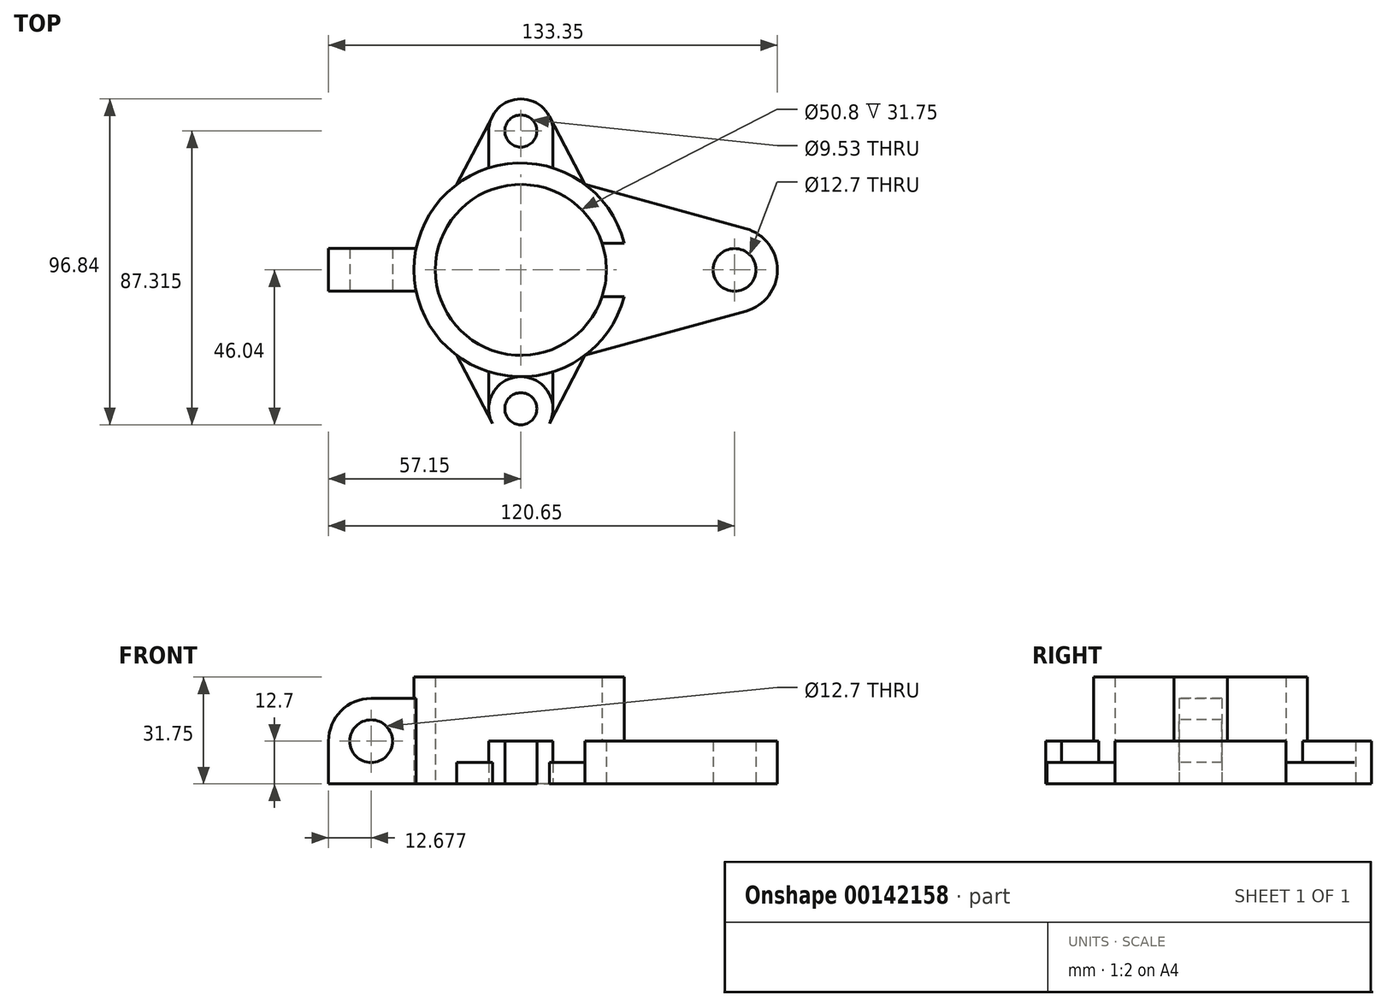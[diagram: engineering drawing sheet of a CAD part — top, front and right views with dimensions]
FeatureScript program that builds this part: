
annotation { "Feature Type Name" : "Feature", "Feature Type Description" : "" }
export const myFeature = defineFeature(function(context is Context, id is Id, definition is map)
    precondition{}
    {
        {
            var Q0;
            Q0=qCreatedBy(makeId("Top.planeOp"),FACE);
            var sketch = newSketch(context, id + "F0", { "sketchPlane" : qUnion([Q0])});
            skCircle(sketch, "E0", {"center": v(0, 0) * mm, "radius": 31.75 * mm});
            skCircle(sketch, "E1", {"center": v(0, 0) * mm, "radius": 25.4 * mm});
            skCircle(sketch, "E2", {"center": v(0, 41.28) * mm, "radius": 4.76 * mm});
            skCircle(sketch, "E3", {"center": v(0, 41.28) * mm, "radius": 9.53 * mm});
            skLineSegment(sketch, "E4", {"start": v(19.05, 25.4) * mm, "end": v(8.44, 45.69) * mm});
            skLineSegment(sketch, "E5.MirrorCS", {"start": v(-19.05, 25.4) * mm, "end": v(-8.44, 45.69) * mm});
            skLineSegment(sketch, "E6", {"start": v(9.53, 30.29) * mm, "end": v(9.53, 41.28) * mm});
            skLineSegment(sketch, "E7.MirrorCS", {"start": v(-9.53, 30.29) * mm, "end": v(-9.53, 41.28) * mm});
            skLineSegment(sketch, "E8.MirrorCS", {"start": v(-9.53, -30.29) * mm, "end": v(-9.53, -41.28) * mm});
            skLineSegment(sketch, "E9.MirrorCS", {"start": v(-19.05, -25.4) * mm, "end": v(-8.44, -45.69) * mm});
            skLineSegment(sketch, "E10.MirrorCS", {"start": v(9.53, -30.29) * mm, "end": v(9.53, -41.28) * mm});
            skLineSegment(sketch, "E11.MirrorCS", {"start": v(19.05, -25.4) * mm, "end": v(8.44, -45.69) * mm});
            skCircle(sketch, "E12.MirrorC", {"center": v(0, -41.28) * mm, "radius": 9.53 * mm});
            skCircle(sketch, "E13.MirrorC", {"center": v(0, -41.28) * mm, "radius": 4.76 * mm});
            skArc(sketch, "E14", {"start": v(66.87, -12.25) * mm, "mid": v(76.2, 0) * mm, "end": v(66.87, 12.25) * mm});
            skCircle(sketch, "E15", {"center": v(63.5, 0) * mm, "radius": 6.35 * mm});
            skLineSegment(sketch, "E16", {"start": v(19.05, -25.4) * mm, "end": v(66.87, -12.25) * mm});
            skLineSegment(sketch, "E17.MirrorCS", {"start": v(19.05, 25.4) * mm, "end": v(66.87, 12.25) * mm});
            skLineSegment(sketch, "E18.0", {"start": v(-31.1, 6.35) * mm, "end": v(-57.15, 6.35) * mm});
            skCircle(sketch, "E19", {"center": v(0, 0) * mm, "radius": 44.45 * mm, "construction": true});
            skCircle(sketch, "E20", {"center": v(-44.45, 0) * mm, "radius": 12.7 * mm, "construction": true});
            skLineSegment(sketch, "E21", {"start": v(-57.15, 0) * mm, "end": v(-57.15, 6.35) * mm});
            skLineSegment(sketch, "E22.MirrorCS", {"start": v(-57.15, 0) * mm, "end": v(-57.15, -6.35) * mm});
            skLineSegment(sketch, "E23.MirrorCS", {"start": v(-31.1, -6.35) * mm, "end": v(-57.15, -6.35) * mm});
            skSolve(sketch);
        }
        {
            var Q0;
            Q0=makeQuery(id+"F0.imprint","IMPRINT",FACE,{"disambiguationData":[TD([[makeQuery(id+"F0.imprint","IMPRINT",EDGE,{"derivedFrom":sQuery(id+"F0.wireOp",EDGE,"E1")}),-1.0]])]});
            extrude(context, id + "F1", {"entities" : qUnion([Q0]), "depth" : 31.75 * mm});
        }
        {
            var Q0;
            Q0=makeQuery(id+"F0.imprint","IMPRINT",FACE,{"disambiguationData":[TD([[makeQuery(id+"F0.imprint","IMPRINT",EDGE,{"derivedFrom":sQuery(id+"F0.wireOp",EDGE,"E2")}),-1.0]])]});
            var Q1;
            {var subQ0=sQuery(id+"F0.wireOp",EDGE,"E6");Q1=makeQuery(id+"F0.imprint","IMPRINT",FACE,{"disambiguationData":[TD([[makeQuery(id+"F0.imprint","IMPRINT",EDGE,{"derivedFrom":subQ0}),1.0]])]});}
            var Q2;
            {var subQ0=sQuery(id+"F0.wireOp",EDGE,"E10.MirrorCS");Q2=makeQuery(id+"F0.imprint","IMPRINT",FACE,{"disambiguationData":[TD([[makeQuery(id+"F0.imprint","IMPRINT",EDGE,{"derivedFrom":subQ0}),-1.0]])]});}
            var Q3;
            {var subQ0=sQuery(id+"F0.wireOp",EDGE,"E8.MirrorCS");Q3=makeQuery(id+"F0.imprint","IMPRINT",FACE,{"disambiguationData":[TD([[makeQuery(id+"F0.imprint","IMPRINT",EDGE,{"derivedFrom":subQ0}),1.0]])]});}
            var Q4;
            Q4=makeQuery(id+"F0.imprint","IMPRINT",FACE,{"disambiguationData":[TD([[makeQuery(id+"F0.imprint","IMPRINT",EDGE,{"derivedFrom":sQuery(id+"F0.wireOp",EDGE,"E13.MirrorC")}),1.0]])]});
            var Q5;
            {var subQ0=sQuery(id+"F0.wireOp",EDGE,"E7.MirrorCS");Q5=makeQuery(id+"F0.imprint","IMPRINT",FACE,{"disambiguationData":[TD([[makeQuery(id+"F0.imprint","IMPRINT",EDGE,{"derivedFrom":subQ0}),-1.0]])]});}
            var Q6;
            Q6=makeQuery(id+"F0.imprint","IMPRINT",FACE,{"disambiguationData":[TD([[makeQuery(id+"F0.imprint","IMPRINT",EDGE,{"derivedFrom":sQuery(id+"F0.wireOp",EDGE,"E14")}),1.0]])]});
            extrude(context, id + "F2", {"entities" : qUnion([Q0, Q1, Q2, Q3, Q4, Q5, Q6]), "operationType" : NewBodyOperationType.ADD, "depth" : 12.7 * mm});
        }
        {
            var Q0;
            {var subQ0=sQuery(id+"F0.wireOp",EDGE,"E5.MirrorCS");Q0=makeQuery(id+"F0.imprint","IMPRINT",FACE,{"disambiguationData":[TD([[makeQuery(id+"F0.imprint","IMPRINT",EDGE,{"derivedFrom":subQ0}),-1.0]])]});}
            var Q1;
            {var subQ0=sQuery(id+"F0.wireOp",EDGE,"E4");Q1=makeQuery(id+"F0.imprint","IMPRINT",FACE,{"disambiguationData":[TD([[makeQuery(id+"F0.imprint","IMPRINT",EDGE,{"derivedFrom":subQ0}),1.0]])]});}
            var Q2;
            {var subQ0=sQuery(id+"F0.wireOp",EDGE,"E10.MirrorCS");Q2=makeQuery(id+"F0.imprint","IMPRINT",FACE,{"disambiguationData":[TD([[makeQuery(id+"F0.imprint","IMPRINT",EDGE,{"derivedFrom":subQ0}),1.0]])]});}
            var Q3;
            {var subQ0=sQuery(id+"F0.wireOp",EDGE,"E8.MirrorCS");Q3=makeQuery(id+"F0.imprint","IMPRINT",FACE,{"disambiguationData":[TD([[makeQuery(id+"F0.imprint","IMPRINT",EDGE,{"derivedFrom":subQ0}),-1.0]])]});}
            extrude(context, id + "F3", {"entities" : qUnion([Q0, Q1, Q2, Q3]), "operationType" : NewBodyOperationType.ADD, "depth" : 6.35 * mm});
        }
        {
            var Q0;
            {var subQ0=sQuery(id+"F0.wireOp",EDGE,"E18.0");Q0=makeQuery(id+"F0.imprint","IMPRINT",FACE,{"disambiguationData":[TD([[makeQuery(id+"F0.imprint","IMPRINT",EDGE,{"derivedFrom":subQ0}),1.0]])]});}
            extrude(context, id + "F4", {"entities" : qUnion([Q0]), "depth" : 25.4 * mm});
        }
        {
            var Q0;
            Q0=qCreatedBy(makeId("Front.planeOp"),FACE);
            var sketch = newSketch(context, id + "F5", { "sketchPlane" : qUnion([Q0])});
            skCircle(sketch, "E24", {"center": v(-44.47, 12.7) * mm, "radius": 6.35 * mm});
            skSolve(sketch);
        }
        {
            var Q0;
            Q0 = qSketchRegion(id + "F5", true);
            extrude(context, id + "F6", {"entities" : qUnion([Q0]), "operationType" : NewBodyOperationType.REMOVE, "endBound" : BoundingType.SYMMETRIC, "oppositeDirection" : true, "depth" : 12.7 * mm});
        }
        {
            var Q0;
            Q0 = qSketchRegion(id + "F5", true);
            extrude(context, id + "F7", {"entities" : qUnion([Q0]), "operationType" : NewBodyOperationType.REMOVE, "endBound" : BoundingType.SYMMETRIC, "oppositeDirection" : true, "depth" : 12.7 * mm});
        }
        {
            var Q0;
            Q0=makeQuery(id+"F4.opExtrude","CAP_EDGE",EDGE,{"disambiguationData":[OSD([sQuery(id+"F0.wireOp",EDGE,"E21"),sQuery(id+"F0.wireOp",EDGE,"E22.MirrorCS")])],"isStart":false});
            fillet(context, id + "F8", {"entities" : qUnion([Q0]), "radius" : 12.7 * mm, "tangentPropagation" : true, "allowEdgeOverflow" : false});
        }
        {
            var Q0;
            Q0=qCreatedBy(makeId("Right.planeOp"),FACE);
            var sketch = newSketch(context, id + "F9", { "sketchPlane" : qUnion([Q0])});
            skLineSegment(sketch, "E25.0", {"start": v(-7.94, 31.75) * mm, "end": v(7.94, 31.75) * mm});
            skLineSegment(sketch, "E26", {"start": v(0, 31.75) * mm, "end": v(7.94, 31.75) * mm});
            skLineSegment(sketch, "E27", {"start": v(7.94, 31.75) * mm, "end": v(7.94, 31.75) * mm});
            skLineSegment(sketch, "E28.MirrorCS", {"start": v(0, 31.75) * mm, "end": v(-7.94, 31.75) * mm});
            skLineSegment(sketch, "E29.MirrorCS", {"start": v(-7.94, 12.7) * mm, "end": v(-7.94, 31.75) * mm});
            skPoint(sketch, "E30.orphan", {"position": v(25.4, 31.75) * mm});
            skPoint(sketch, "E31.orphan", {"position": v(-25.4, 31.75) * mm});
            skPoint(sketch, "E32.start.orphan", {"position": v(0, 31.75) * mm});
            skLineSegment(sketch, "E33", {"start": v(7.94, 31.75) * mm, "end": v(7.94, 12.7) * mm});
            skLineSegment(sketch, "E34", {"start": v(7.94, 12.7) * mm, "end": v(-7.94, 12.7) * mm});
            skSolve(sketch);
        }
        {
            var Q0;
            Q0 = qSketchRegion(id + "F9", true);
            extrude(context, id + "F10", {"entities" : qUnion([Q0]), "operationType" : NewBodyOperationType.REMOVE, "depth" : 31.75 * mm});
        }
        {
            var Q0;
            Q0 = qSketchRegion(id + "F9", true);
            extrude(context, id + "F11", {"entities" : qUnion([Q0]), "operationType" : NewBodyOperationType.REMOVE, "depth" : 63.5 * mm});
        }
    });
